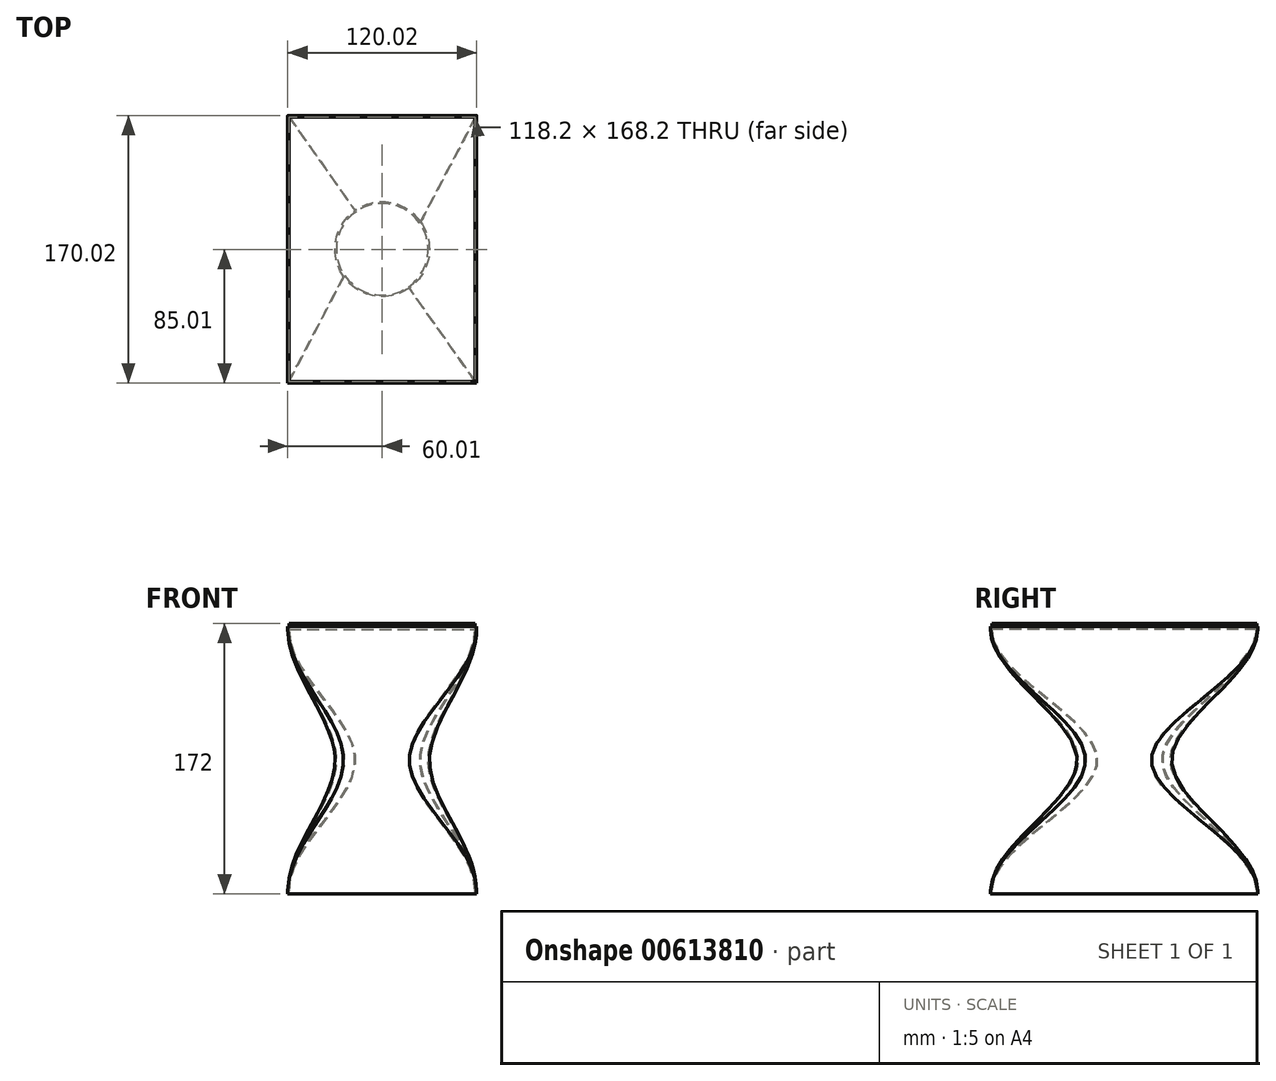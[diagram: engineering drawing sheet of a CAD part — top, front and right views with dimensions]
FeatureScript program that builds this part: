
annotation { "Feature Type Name" : "Feature", "Feature Type Description" : "" }
export const myFeature = defineFeature(function(context is Context, id is Id, definition is map)
    precondition{}
    {
        {
            var Q0;
            Q0=qCreatedBy(makeId("Top.planeOp"),FACE);
            var sketch = newSketch(context, id + "F0", { "sketchPlane" : qUnion([Q0])});
            skLineSegment(sketch, "E0.bottom", {"start": v(-60, 85) * mm, "end": v(60, 85) * mm});
            skLineSegment(sketch, "E0.top", {"start": v(-60, -85) * mm, "end": v(60, -85) * mm});
            skLineSegment(sketch, "E0.left", {"start": v(-60, 85) * mm, "end": v(-60, -85) * mm});
            skLineSegment(sketch, "E0.right", {"start": v(60, 85) * mm, "end": v(60, -85) * mm});
            skPoint(sketch, "E0.middle", {"position": v(0, 0) * mm});
            skSolve(sketch);
        }
        {
            var Q0;
            Q0=qCreatedBy(makeId("Top.planeOp"),FACE);
            cPlane(context, id + "F1", {"entities" : qUnion([Q0]), "cplaneType" : CPlaneType.OFFSET, "offset" : 2 * mm, "width" : 150 * mm, "height" : 150 * mm});
        }
        {
            var Q0;
            Q0=qCreatedBy(id+"F1.planeOp",FACE);
            var sketch = newSketch(context, id + "F2", { "sketchPlane" : qUnion([Q0])});
            skLineSegment(sketch, "E1.bottom", {"start": v(-60, 85) * mm, "end": v(60, 85) * mm});
            skLineSegment(sketch, "E1.top", {"start": v(-60, -85) * mm, "end": v(60, -85) * mm});
            skLineSegment(sketch, "E1.left", {"start": v(-60, 85) * mm, "end": v(-60, -85) * mm});
            skLineSegment(sketch, "E1.right", {"start": v(60, 85) * mm, "end": v(60, -85) * mm});
            skPoint(sketch, "E1.middle", {"position": v(0, 0) * mm});
            skSolve(sketch);
        }
        {
            var Q0;
            Q0=qCreatedBy(makeId("Top.planeOp"),FACE);
            cPlane(context, id + "F3", {"entities" : qUnion([Q0]), "cplaneType" : CPlaneType.OFFSET, "offset" : 85 * mm, "width" : 150 * mm, "height" : 150 * mm});
        }
        {
            var Q0;
            Q0=qCreatedBy(makeId("Top.planeOp"),FACE);
            cPlane(context, id + "F4", {"entities" : qUnion([Q0]), "cplaneType" : CPlaneType.OFFSET, "offset" : 168 * mm, "width" : 150 * mm, "height" : 150 * mm});
        }
        {
            var Q0;
            Q0=qCreatedBy(makeId("Top.planeOp"),FACE);
            cPlane(context, id + "F5", {"entities" : qUnion([Q0]), "cplaneType" : CPlaneType.OFFSET, "offset" : 170 * mm, "width" : 150 * mm, "height" : 150 * mm});
        }
        {
            var Q0;
            Q0=qCreatedBy(id+"F3.planeOp",FACE);
            var sketch = newSketch(context, id + "F6", { "sketchPlane" : qUnion([Q0])});
            skCircle(sketch, "E2", {"center": v(0, 0) * mm, "radius": 30 * mm});
            skSolve(sketch);
        }
        {
            var Q0;
            Q0=qCreatedBy(id+"F3.planeOp",FACE);
            var sketch = newSketch(context, id + "F7", { "sketchPlane" : qUnion([Q0])});
            skCircle(sketch, "E3", {"center": v(0, 0) * mm, "radius": 29.1 * mm});
            skSolve(sketch);
        }
        {
            var Q0;
            Q0=qCreatedBy(id+"F4.planeOp",FACE);
            var sketch = newSketch(context, id + "F8", { "sketchPlane" : qUnion([Q0])});
            skLineSegment(sketch, "E4.bottom", {"start": v(-60, 85) * mm, "end": v(60, 85) * mm});
            skLineSegment(sketch, "E4.top", {"start": v(-60, -85) * mm, "end": v(60, -85) * mm});
            skLineSegment(sketch, "E4.left", {"start": v(-60, 85) * mm, "end": v(-60, -85) * mm});
            skLineSegment(sketch, "E4.right", {"start": v(60, 85) * mm, "end": v(60, -85) * mm});
            skPoint(sketch, "E4.middle", {"position": v(0, 0) * mm});
            skSolve(sketch);
        }
        {
            var Q0;
            Q0=qCreatedBy(id+"F5.planeOp",FACE);
            var sketch = newSketch(context, id + "F9", { "sketchPlane" : qUnion([Q0])});
            skLineSegment(sketch, "E5.bottom", {"start": v(-60, 85) * mm, "end": v(60, 85) * mm});
            skLineSegment(sketch, "E5.top", {"start": v(-60, -85) * mm, "end": v(60, -85) * mm});
            skLineSegment(sketch, "E5.left", {"start": v(-60, 85) * mm, "end": v(-60, -85) * mm});
            skLineSegment(sketch, "E5.right", {"start": v(60, 85) * mm, "end": v(60, -85) * mm});
            skPoint(sketch, "E5.middle", {"position": v(0, 0) * mm});
            skSolve(sketch);
        }
        {
            var Q0;
            Q0=qCreatedBy(id+"F5.planeOp",FACE);
            var sketch = newSketch(context, id + "F10", { "sketchPlane" : qUnion([Q0])});
            skLineSegment(sketch, "E6.bottom", {"start": v(-59.1, 84.1) * mm, "end": v(59.1, 84.1) * mm});
            skLineSegment(sketch, "E6.top", {"start": v(-59.1, -84.1) * mm, "end": v(59.1, -84.1) * mm});
            skLineSegment(sketch, "E6.left", {"start": v(-59.1, 84.1) * mm, "end": v(-59.1, -84.1) * mm});
            skLineSegment(sketch, "E6.right", {"start": v(59.1, 84.1) * mm, "end": v(59.1, -84.1) * mm});
            skPoint(sketch, "E6.middle", {"position": v(0, 0) * mm});
            skSolve(sketch);
        }
        {
            var Q0;
            Q0=qCreatedBy(id+"F4.planeOp",FACE);
            var sketch = newSketch(context, id + "F11", { "sketchPlane" : qUnion([Q0])});
            skLineSegment(sketch, "E7.bottom", {"start": v(-59.1, 84.1) * mm, "end": v(59.1, 84.1) * mm});
            skLineSegment(sketch, "E7.top", {"start": v(-59.1, -84.1) * mm, "end": v(59.1, -84.1) * mm});
            skLineSegment(sketch, "E7.left", {"start": v(-59.1, 84.1) * mm, "end": v(-59.1, -84.1) * mm});
            skLineSegment(sketch, "E7.right", {"start": v(59.1, 84.1) * mm, "end": v(59.1, -84.1) * mm});
            skPoint(sketch, "E7.middle", {"position": v(0, 0) * mm});
            skSolve(sketch);
        }
        {
            var Q0;
            Q0=qCreatedBy(makeId("Top.planeOp"),FACE);
            var sketch = newSketch(context, id + "F12", { "sketchPlane" : qUnion([Q0])});
            skLineSegment(sketch, "E8.bottom", {"start": v(-59.1, 84.1) * mm, "end": v(59.1, 84.1) * mm});
            skLineSegment(sketch, "E8.top", {"start": v(-59.1, -84.1) * mm, "end": v(59.1, -84.1) * mm});
            skLineSegment(sketch, "E8.left", {"start": v(-59.1, 84.1) * mm, "end": v(-59.1, -84.1) * mm});
            skLineSegment(sketch, "E8.right", {"start": v(59.1, 84.1) * mm, "end": v(59.1, -84.1) * mm});
            skPoint(sketch, "E8.middle", {"position": v(0, 0) * mm});
            skSolve(sketch);
        }
        {
            var Q0;
            Q0=qCreatedBy(id+"F1.planeOp",FACE);
            var sketch = newSketch(context, id + "F13", { "sketchPlane" : qUnion([Q0])});
            skLineSegment(sketch, "E9.bottom", {"start": v(-59.1, 84.1) * mm, "end": v(59.1, 84.1) * mm});
            skLineSegment(sketch, "E9.top", {"start": v(-59.1, -84.1) * mm, "end": v(59.1, -84.1) * mm});
            skLineSegment(sketch, "E9.left", {"start": v(-59.1, 84.1) * mm, "end": v(-59.1, -84.1) * mm});
            skLineSegment(sketch, "E9.right", {"start": v(59.1, 84.1) * mm, "end": v(59.1, -84.1) * mm});
            skPoint(sketch, "E9.middle", {"position": v(0, 0) * mm});
            skSolve(sketch);
        }
        {
            var Q0;
            Q0=makeQuery(id+"F0.imprint","IMPRINT",FACE,{"disambiguationData":[TD([[makeQuery(id+"F0.imprint","IMPRINT",EDGE,{"derivedFrom":sQuery(id+"F0.wireOp",EDGE,"E0.bottom")}),-1.0]])]});
            var Q1;
            Q1=makeQuery(id+"F2.imprint","IMPRINT",FACE,{"disambiguationData":[TD([[makeQuery(id+"F2.imprint","IMPRINT",EDGE,{"derivedFrom":sQuery(id+"F2.wireOp",EDGE,"E1.bottom")}),-1.0]])]});
            var Q2;
            Q2=makeQuery(id+"F6.imprint","IMPRINT",FACE,{"disambiguationData":[TD([[makeQuery(id+"F6.imprint","IMPRINT",EDGE,{"derivedFrom":sQuery(id+"F6.wireOp",EDGE,"E2")}),1.0]])]});
            var Q3;
            Q3=makeQuery(id+"F8.imprint","IMPRINT",FACE,{"disambiguationData":[TD([[makeQuery(id+"F8.imprint","IMPRINT",EDGE,{"derivedFrom":sQuery(id+"F8.wireOp",EDGE,"E4.bottom")}),-1.0]])]});
            var Q4;
            Q4=makeQuery(id+"F9.imprint","IMPRINT",FACE,{"disambiguationData":[TD([[makeQuery(id+"F9.imprint","IMPRINT",EDGE,{"derivedFrom":sQuery(id+"F9.wireOp",EDGE,"E5.bottom")}),-1.0]])]});
            loft(context, id + "F14", {"sheetProfilesArray" : [{ "sheetProfileEntities" : qUnion([Q0]) }, { "sheetProfileEntities" : qUnion([Q1]) }, { "sheetProfileEntities" : qUnion([Q2]) }, { "sheetProfileEntities" : qUnion([Q3]) }, { "sheetProfileEntities" : qUnion([Q4]) }]});
        }
        {
            var Q0;
            Q0=makeQuery(id+"F12.imprint","IMPRINT",FACE,{"disambiguationData":[TD([[makeQuery(id+"F12.imprint","IMPRINT",EDGE,{"derivedFrom":sQuery(id+"F12.wireOp",EDGE,"E8.bottom")}),-1.0]])]});
            var Q1;
            Q1=makeQuery(id+"F13.imprint","IMPRINT",FACE,{"disambiguationData":[TD([[makeQuery(id+"F13.imprint","IMPRINT",EDGE,{"derivedFrom":sQuery(id+"F13.wireOp",EDGE,"E9.bottom")}),-1.0]])]});
            var Q2;
            Q2=makeQuery(id+"F7.imprint","IMPRINT",FACE,{"disambiguationData":[TD([[makeQuery(id+"F7.imprint","IMPRINT",EDGE,{"derivedFrom":sQuery(id+"F7.wireOp",EDGE,"E3")}),1.0]])]});
            var Q3;
            Q3=makeQuery(id+"F11.imprint","IMPRINT",FACE,{"disambiguationData":[TD([[makeQuery(id+"F11.imprint","IMPRINT",EDGE,{"derivedFrom":sQuery(id+"F11.wireOp",EDGE,"E7.bottom")}),-1.0]])]});
            var Q4;
            Q4=makeQuery(id+"F10.imprint","IMPRINT",FACE,{"disambiguationData":[TD([[makeQuery(id+"F10.imprint","IMPRINT",EDGE,{"derivedFrom":sQuery(id+"F10.wireOp",EDGE,"E6.bottom")}),-1.0]])]});
            loft(context, id + "F15", {"sheetProfilesArray" : [{ "sheetProfileEntities" : qUnion([Q0]) }, { "sheetProfileEntities" : qUnion([Q1]) }, { "sheetProfileEntities" : qUnion([Q2]) }, { "sheetProfileEntities" : qUnion([Q3]) }, { "sheetProfileEntities" : qUnion([Q4]) }]});
        }
        {
            var Q0;
            Q0=makeQuery(id+"F15.opLoft","SWEPT_BODY",BODY,{"disambiguationData":[OSD([sQuery(id+"F7.wireOp",EDGE,"E3"),makeQuery(id+"F10.imprint","IMPRINT",FACE,{"disambiguationData":[TD([[makeQuery(id+"F10.imprint","IMPRINT",EDGE,{"derivedFrom":sQuery(id+"F10.wireOp",EDGE,"E6.bottom")}),-1.0]])]}),sQuery(id+"F11.wireOp",EDGE,"E7.left"),makeQuery(id+"F12.imprint","IMPRINT",FACE,{"disambiguationData":[TD([[makeQuery(id+"F12.imprint","IMPRINT",EDGE,{"derivedFrom":sQuery(id+"F12.wireOp",EDGE,"E8.bottom")}),-1.0]])]}),sQuery(id+"F13.wireOp",EDGE,"E9.left")])]});
            var Q1;
            Q1=makeQuery(id+"F14.opLoft","SWEPT_BODY",BODY,{"disambiguationData":[OSD([makeQuery(id+"F0.imprint","IMPRINT",FACE,{"disambiguationData":[TD([[makeQuery(id+"F0.imprint","IMPRINT",EDGE,{"derivedFrom":sQuery(id+"F0.wireOp",EDGE,"E0.bottom")}),-1.0]])]}),sQuery(id+"F2.wireOp",EDGE,"E1.left"),sQuery(id+"F6.wireOp",EDGE,"E2"),sQuery(id+"F8.wireOp",EDGE,"E4.left"),makeQuery(id+"F9.imprint","IMPRINT",FACE,{"disambiguationData":[TD([[makeQuery(id+"F9.imprint","IMPRINT",EDGE,{"derivedFrom":sQuery(id+"F9.wireOp",EDGE,"E5.bottom")}),-1.0]])]})])]});
            booleanBodies(context, id + "F16", {"operationType" : BooleanOperationType.SUBTRACTION, "tools" : qUnion([Q0]), "targets" : qUnion([Q1])});
        }
        {
            var Q0;
            Q0=makeQuery(id+"F10.imprint","IMPRINT",FACE,{"disambiguationData":[TD([[makeQuery(id+"F10.imprint","IMPRINT",EDGE,{"derivedFrom":sQuery(id+"F10.wireOp",EDGE,"E6.bottom")}),-1.0]])]});
            extrude(context, id + "F17", {"entities" : qUnion([Q0]), "endBound" : BoundingType.SYMMETRIC, "depth" : 4 * mm, "offsetDistance" : 25 * mm});
        }
    });
